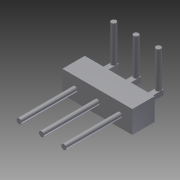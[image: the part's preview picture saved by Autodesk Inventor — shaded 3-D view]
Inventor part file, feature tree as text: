
AUTODESK INVENTOR PART (.ipt)
format: ipt  version: 2013 (Build 170138000, 138)  size: 97,792 bytes
history: native  units: mm
features: extrude x1, imported_body x1
ambient origin geometry x8: Origin, YZ Plane, XZ Plane, XY Plane, X Axis, Y Axis, Z Axis, Center Point
feature tree (2):
  extrude  "Extrude4"  [1 undecoded]
  imported_body  "Base1"
note: 1 required parameter value undecoded (feature->parameter linkage not recoverable at this tier; creation-order binding heuristic only, values carry confidence <= 0.55)
